# Revit family: ITK_ Разветвитель (Y-адаптер) кат. 5Е 2xRJ45-1хRJ45
name_source: partatom
category: Обобщенные модели
units: mm (PartAtom-declared; Revit-internal decimal feet)

## family parameters
Всегда вертикально = Да
Может служить основой для арматурных стержней = Нет
На основе рабочей плоскости = Нет
Общий = Нет
При загрузке вырезать с полостями = Нет
Размер круглого соединителя = Использовать диаметр
Тип детали = Нормальный
Точка расчета площади = Нет

## types (1)
- CS7-1C5EU-Y2-1
    ADSK_URL страницы изделия = https://www.itk-group.ru
    ADSK_Версия Revit = 2019
    ADSK_Версия семейства = 1.0
    ADSK_Группирование = I. ЩИТЫ И ПУЛЬТЫ
    ADSK_Единица измерения = шт
    ADSK_Завод-изготовитель = IEK
    ADSK_Код изделия = CS7-1C5EU-Y2-1
    ADSK_Масса = 0
    ADSK_Материал наименование = Пластик
    ADSK_Наименование = ITK Разветвитель (Y-адаптер) кат. 5Е 2xRJ45-1хRJ45
    IEK_URL = https://www.itk-group.ru
    IEK_Описание = Соответствие международным стандартам качества, что обеспечивает совместимость с компонентами и с кабелем.
Изготовлены из высококачественных негорючих материалов и отличаются надежностью и удобством эксплуатации.
    IEK_Цена за единицу = 290.56
    KSI_CMa_Строительные материалы = 01.7.14.03
    KSI_CPr_Строительные изделия = 27.33.13.61.1.04.09-1002 27.33.13.61.1.04.09-1004 27.33.13.61.1.04.09-1006 27.33.13.61.1.04.09-1008 27.33.13.61.1.04.09-1010 27.33.13.61.1.04.09-1012 27.33.13.61.1.04.09-1014 27.33.13.61.1.04.09-1016 27.33.13.61.1.04.09-1018 27.33.13.61.1.04.09-1020 27.33.13.61.1.04.09-1022 27.33.13.61.1.04.09-1024 27.33.13.61.1.04.09-1026 27.33.13.61.1.04.09-1028 27.33.13.61.1.04.09-1030 27.33.13.61.1.04.09-1032 27.33.13.61.1.04.09-1034 27.33.13.61.1.04.09-1036
    URL = https://www.iek.ru
    Высота = 24 мм
    Глубина = 189 мм
    Изготовитель = ITK
    Материал = Окраска - RAL 9005
    Ширина = 68 мм
